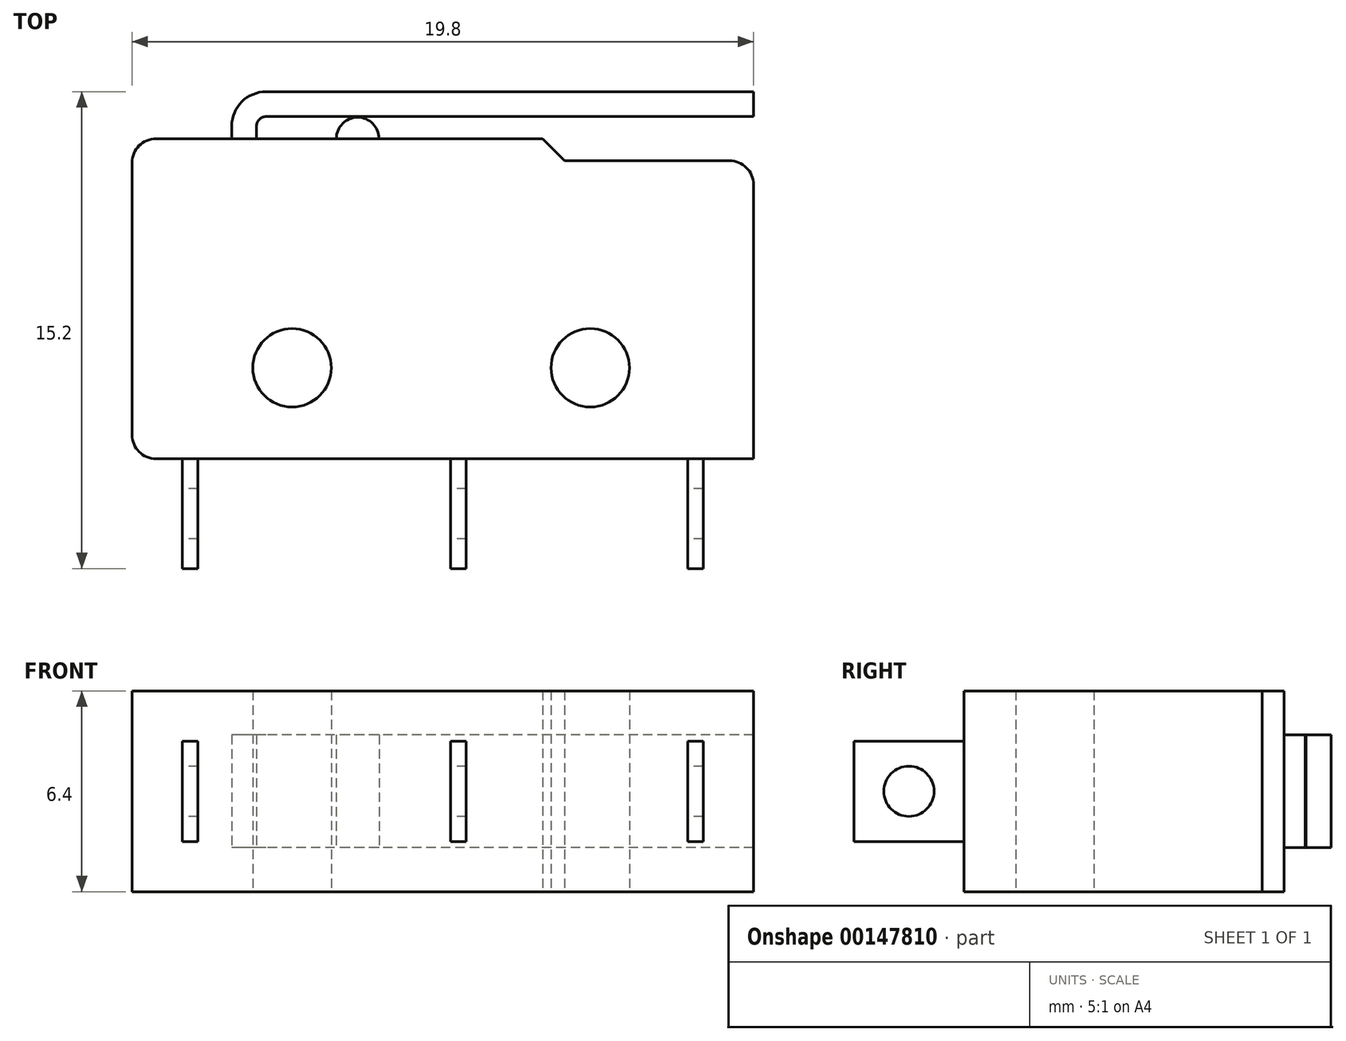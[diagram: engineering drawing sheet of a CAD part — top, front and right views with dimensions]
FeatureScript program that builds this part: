
annotation { "Feature Type Name" : "Feature", "Feature Type Description" : "" }
export const myFeature = defineFeature(function(context is Context, id is Id, definition is map)
    precondition{}
    {
        {
            var Q0;
            Q0=qCreatedBy(makeId("Top.planeOp"),FACE);
            var sketch = newSketch(context, id + "F0", { "sketchPlane" : qUnion([Q0])});
            skLineSegment(sketch, "E0", {"start": v(0, 0) * mm, "end": v(6.02, 0) * mm});
            skLineSegment(sketch, "E1", {"start": v(6.02, 0) * mm, "end": v(6.02, -9.5) * mm});
            skLineSegment(sketch, "E2", {"start": v(0, 0) * mm, "end": v(-0.7, 0.7) * mm});
            skLineSegment(sketch, "E3", {"start": v(6.02, 0) * mm, "end": v(6.02, 0.7) * mm, "construction": true});
            skLineSegment(sketch, "E4", {"start": v(-0.7, 0.7) * mm, "end": v(6.02, 0.7) * mm, "construction": true});
            skLineSegment(sketch, "E5.bottom", {"start": v(4.42, -9.5) * mm, "end": v(3.92, -9.5) * mm});
            skLineSegment(sketch, "E5.top", {"start": v(4.42, -13) * mm, "end": v(3.92, -13) * mm});
            skLineSegment(sketch, "E5.left", {"start": v(3.92, -9.5) * mm, "end": v(3.92, -13) * mm});
            skLineSegment(sketch, "E5.right", {"start": v(4.42, -9.5) * mm, "end": v(4.42, -13) * mm});
            skLineSegment(sketch, "E6.bottom", {"start": v(-3.13, -9.5) * mm, "end": v(-3.63, -9.5) * mm});
            skLineSegment(sketch, "E6.top", {"start": v(-3.13, -13) * mm, "end": v(-3.63, -13) * mm});
            skLineSegment(sketch, "E6.left", {"start": v(-3.13, -9.5) * mm, "end": v(-3.13, -13) * mm});
            skLineSegment(sketch, "E6.right", {"start": v(-3.63, -9.5) * mm, "end": v(-3.63, -13) * mm});
            skLineSegment(sketch, "E7.top", {"start": v(-11.68, -13) * mm, "end": v(-12.18, -13) * mm});
            skLineSegment(sketch, "E7.left", {"start": v(-12.18, -9.5) * mm, "end": v(-12.18, -13) * mm});
            skLineSegment(sketch, "E7.right", {"start": v(-11.68, -9.5) * mm, "end": v(-11.68, -13) * mm});
            skLineSegment(sketch, "E8", {"start": v(-0.7, 0.7) * mm, "end": v(-5.91, 0.7) * mm});
            skLineSegment(sketch, "E9", {"start": v(-5.91, 0.7) * mm, "end": v(-7.27, 0.7) * mm, "construction": true});
            skArc(sketch, "E10", {"start": v(-5.91, 0.7) * mm, "mid": v(-6.6, 1.38) * mm, "end": v(-7.27, 0.7) * mm});
            skLineSegment(sketch, "E11", {"start": v(-7.27, 0.7) * mm, "end": v(-9.81, 0.7) * mm});
            skLineSegment(sketch, "E12", {"start": v(-9.81, 0.7) * mm, "end": v(-9.81, 1.1) * mm});
            skArc(sketch, "E13", {"start": v(-9.51, 1.4) * mm, "mid": v(-9.73, 1.32) * mm, "end": v(-9.81, 1.1) * mm});
            skLineSegment(sketch, "E14", {"start": v(-9.51, 1.4) * mm, "end": v(6.02, 1.4) * mm});
            skLineSegment(sketch, "E15", {"start": v(6.02, 1.4) * mm, "end": v(6.02, 2.2) * mm});
            skLineSegment(sketch, "E16", {"start": v(6.02, 2.2) * mm, "end": v(-9.51, 2.2) * mm});
            skArc(sketch, "E17", {"start": v(-9.51, 2.2) * mm, "mid": v(-10.29, 1.88) * mm, "end": v(-10.6, 1.1) * mm});
            skLineSegment(sketch, "E18", {"start": v(-10.6, 1.1) * mm, "end": v(-10.6, 0.7) * mm});
            skLineSegment(sketch, "E19", {"start": v(-10.6, 0.7) * mm, "end": v(-9.81, 0.7) * mm});
            skLineSegment(sketch, "E20", {"start": v(-8.68, -9.5) * mm, "end": v(-8.68, -6.6) * mm, "construction": true});
            skLineSegment(sketch, "E21", {"start": v(-8.68, -6.6) * mm, "end": v(-13.78, -6.6) * mm, "construction": true});
            skLineSegment(sketch, "E22", {"start": v(-13.78, -9.5) * mm, "end": v(-13.78, 0.7) * mm});
            skCircle(sketch, "E23", {"center": v(-8.68, -6.6) * mm, "radius": 1.25 * mm});
            skLineSegment(sketch, "E24", {"start": v(-8.68, -6.6) * mm, "end": v(0.82, -6.6) * mm, "construction": true});
            skCircle(sketch, "E25", {"center": v(0.82, -6.6) * mm, "radius": 1.25 * mm});
            skLineSegment(sketch, "E26", {"start": v(-13.78, -9.5) * mm, "end": v(-12.18, -9.5) * mm});
            skLineSegment(sketch, "E27", {"start": v(-12.18, -9.5) * mm, "end": v(-11.68, -9.5) * mm});
            skLineSegment(sketch, "E28", {"start": v(-11.68, -9.5) * mm, "end": v(-3.63, -9.5) * mm});
            skPoint(sketch, "E29", {"position": v(-3.38, -13) * mm});
            skLineSegment(sketch, "E30", {"start": v(6.02, -9.5) * mm, "end": v(4.42, -9.5) * mm});
            skLineSegment(sketch, "E31", {"start": v(3.92, -9.5) * mm, "end": v(-3.13, -9.5) * mm});
            skLineSegment(sketch, "E32", {"start": v(-13.78, 0.7) * mm, "end": v(-10.6, 0.7) * mm});
            skSolve(sketch);
        }
        {
            var Q0;
            Q0=makeQuery(id+"F0.imprint","IMPRINT",FACE,{"disambiguationData":[TD([[makeQuery(id+"F0.imprint","IMPRINT",EDGE,{"derivedFrom":sQuery(id+"F0.wireOp",EDGE,"E5.bottom")}),1.0]])]});
            var Q1;
            Q1=makeQuery(id+"F0.imprint","IMPRINT",FACE,{"disambiguationData":[TD([[makeQuery(id+"F0.imprint","IMPRINT",EDGE,{"derivedFrom":sQuery(id+"F0.wireOp",EDGE,"E6.bottom")}),1.0]])]});
            var Q2;
            Q2=makeQuery(id+"F0.imprint","IMPRINT",FACE,{"disambiguationData":[TD([[makeQuery(id+"F0.imprint","IMPRINT",EDGE,{"derivedFrom":sQuery(id+"F0.wireOp",EDGE,"E7.top")}),-1.0]])]});
            var Q3;
            Q3=makeQuery(id+"F0.imprint","IMPRINT",FACE,{"disambiguationData":[TD([[makeQuery(id+"F0.imprint","IMPRINT",EDGE,{"derivedFrom":sQuery(id+"F0.wireOp",EDGE,"E12")}),1.0]])]});
            var Q4;
            Q4=makeQuery(id+"F0.imprint","IMPRINT",FACE,{"disambiguationData":[TD([[makeQuery(id+"F0.imprint","IMPRINT",EDGE,{"derivedFrom":sQuery(id+"F0.wireOp",EDGE,"E0")}),-1.0]])]});
            var Q5;
            {var subQ1=sQuery(id+"F0.wireOp",EDGE,"E11");Q5=makeQuery(id+"F0.imprint","IMPRINT",FACE,{"disambiguationData":[TD([[makeQuery(id+"F0.imprint","IMPRINT",EDGE,{"derivedFrom":subQ1}),-1.0]])]});}
            extrude(context, id + "F1", {"entities" : qUnion([Q0, Q1, Q2, Q3, Q4, Q5]), "depth" : 6.4 * mm});
        }
        {
            var Q0;
            Q0=makeQuery(id+"F1.opExtrude","SWEPT_FACE",FACE,{"disambiguationData":[OSD([sQuery(id+"F0.wireOp",EDGE,"E22")])]});
            var sketch = newSketch(context, id + "F2", { "sketchPlane" : qUnion([Q0])});
            skLineSegment(sketch, "E33.bottom", {"start": v(-0.7, 0) * mm, "end": v(-2.2, 0) * mm});
            skLineSegment(sketch, "E33.top", {"start": v(-0.7, 1.4) * mm, "end": v(-2.2, 1.4) * mm});
            skLineSegment(sketch, "E33.left", {"start": v(-0.7, 0) * mm, "end": v(-0.7, 1.4) * mm});
            skLineSegment(sketch, "E33.right", {"start": v(-2.2, 0) * mm, "end": v(-2.2, 1.4) * mm});
            skLineSegment(sketch, "E34.bottom", {"start": v(-0.7, 6.4) * mm, "end": v(-2.2, 6.4) * mm});
            skLineSegment(sketch, "E34.top", {"start": v(-0.7, 5) * mm, "end": v(-2.2, 5) * mm});
            skLineSegment(sketch, "E34.left", {"start": v(-0.7, 6.4) * mm, "end": v(-0.7, 5) * mm});
            skLineSegment(sketch, "E34.right", {"start": v(-2.2, 6.4) * mm, "end": v(-2.2, 5) * mm});
            skLineSegment(sketch, "E35", {"start": v(-2.2, 1.4) * mm, "end": v(-2.2, 5) * mm, "construction": true});
            skPoint(sketch, "E36", {"position": v(-2.2, 3.2) * mm});
            skLineSegment(sketch, "E37.bottom", {"start": v(9.5, 0) * mm, "end": v(13, 0) * mm});
            skLineSegment(sketch, "E37.top", {"start": v(9.5, 1.6) * mm, "end": v(13, 1.6) * mm});
            skLineSegment(sketch, "E37.left", {"start": v(9.5, 0) * mm, "end": v(9.5, 1.6) * mm});
            skLineSegment(sketch, "E37.right", {"start": v(13, 0) * mm, "end": v(13, 1.6) * mm});
            skLineSegment(sketch, "E38.bottom", {"start": v(9.5, 6.4) * mm, "end": v(13, 6.4) * mm});
            skLineSegment(sketch, "E38.top", {"start": v(9.5, 4.8) * mm, "end": v(13, 4.8) * mm});
            skLineSegment(sketch, "E38.left", {"start": v(9.5, 6.4) * mm, "end": v(9.5, 4.8) * mm});
            skLineSegment(sketch, "E38.right", {"start": v(13, 6.4) * mm, "end": v(13, 4.8) * mm});
            skLineSegment(sketch, "E39", {"start": v(13, 1.6) * mm, "end": v(13, 4.8) * mm, "construction": true});
            skPoint(sketch, "E40", {"position": v(13, 3.2) * mm});
            skLineSegment(sketch, "E41", {"start": v(13, 3.2) * mm, "end": v(9.5, 3.2) * mm, "construction": true});
            skCircle(sketch, "E42", {"center": v(11.25, 3.2) * mm, "radius": 0.8 * mm});
            skSolve(sketch);
        }
        {
            var Q0;
            Q0=qSketchRegion(id+"F2",true);
            var Q1;
            Q1=makeQuery(id+"F1.opExtrude","SWEPT_FACE",FACE,{"disambiguationData":[OSD([sQuery(id+"F0.wireOp",EDGE,"E15")])]});
            extrude(context, id + "F3", {"entities" : qUnion([Q0]), "operationType" : NewBodyOperationType.REMOVE, "endBound" : BoundingType.UP_TO_SURFACE, "oppositeDirection" : true, "endBoundEntityFace" : qUnion([Q1]), "depth" : 25.4 * mm});
        }
        {
            var Q0;
            Q0=makeQuery(id+"F3.boolean.opBoolean","INTERSECT",EDGE,{"derivedFrom":[makeQuery(id+"F3.opExtrude","SWEPT_FACE",FACE,{"disambiguationData":[OSD([sQuery(id+"F2.wireOp",EDGE,"E37.left")])]}),makeQuery(id+"F3.opExtrude","SWEPT_FACE",FACE,{"disambiguationData":[OSD([sQuery(id+"F2.wireOp",EDGE,"E38.left")])]})]});
            var Q1;
            Q1=makeQuery(id+"F1.opExtrude","SWEPT_EDGE",EDGE,{"disambiguationData":[OSD([sQuery(id+"F0.wireOp",EDGE,"E0"),sQuery(id+"F0.wireOp",EDGE,"E1")])]});
            var Q2;
            Q2=makeQuery(id+"F1.opExtrude","SWEPT_EDGE",EDGE,{"disambiguationData":[OSD([sQuery(id+"F0.wireOp",EDGE,"E22"),sQuery(id+"F0.wireOp",EDGE,"E26")])]});
            var Q3;
            Q3=makeQuery(id+"F1.opExtrude","SWEPT_EDGE",EDGE,{"disambiguationData":[OSD([sQuery(id+"F0.wireOp",EDGE,"E22"),sQuery(id+"F0.wireOp",EDGE,"E32")])]});
            fillet(context, id + "F4", {"entities" : qUnion([Q0, Q1, Q2, Q3]), "radius" : 0.76 * mm, "tangentPropagation" : true, "allowEdgeOverflow" : false});
        }
    });
